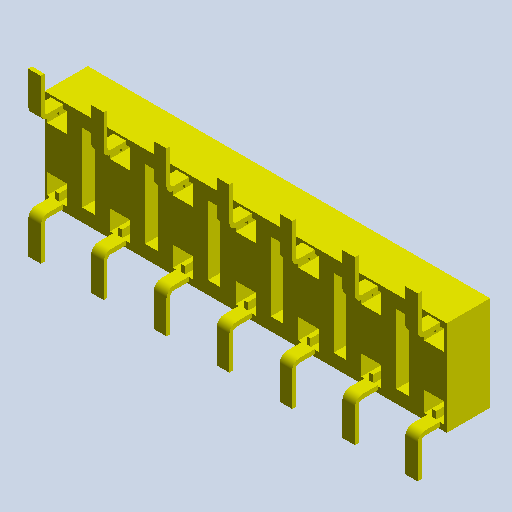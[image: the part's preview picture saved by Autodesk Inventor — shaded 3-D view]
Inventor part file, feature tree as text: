
AUTODESK INVENTOR PART (.ipt)
format: ipt  version: 2024.2 (Build 282272000, 272)  size: 393,728 bytes
history: native  units: mm (DEFAULTED — no unit token found)
features: other x7, extrude x4, sketch x4
ambient origin geometry x8: Origin, YZ Plane, XZ Plane, XY Plane, X Axis, Y Axis, Z Axis, Center Point
bodies: Solid1 (feature_tree)
feature tree (15):
  extrude  "Extrusion1"  Depth=16.256mm TaperAngle=0.0deg
  extrude  "Extrusion2"  Depth=10.16mm TaperAngle=0.0deg
  extrude  "Extrusion3"  [1 undecoded]
  extrude  "Extrusion4"  [1 undecoded]
  other  "pins_to_socket_XY"
  other  "pins_to_socket_YZ"
  other  "pins_to_socket_ZX"
  other  "pins_to_socket_X"
  other  "pins_to_socket_Y"
  other  "pins_to_socket_Z"
  other  "pins_to_socket_Center"
  sketch  "Sketch_11"  dims[d4=16.256mm d5=0.0mm d6=10.16mm d7=0.0mm]
  sketch  "Sketch_12"
  sketch  "Sketch_13"
  sketch  "Sketch_5"  dims[d0=1.7526mm d1=0.0mm d2=16.256mm d3=0.0mm]
note: 2 required parameter values undecoded (feature->parameter linkage not recoverable at this tier; creation-order binding heuristic only, values carry confidence <= 0.55)
